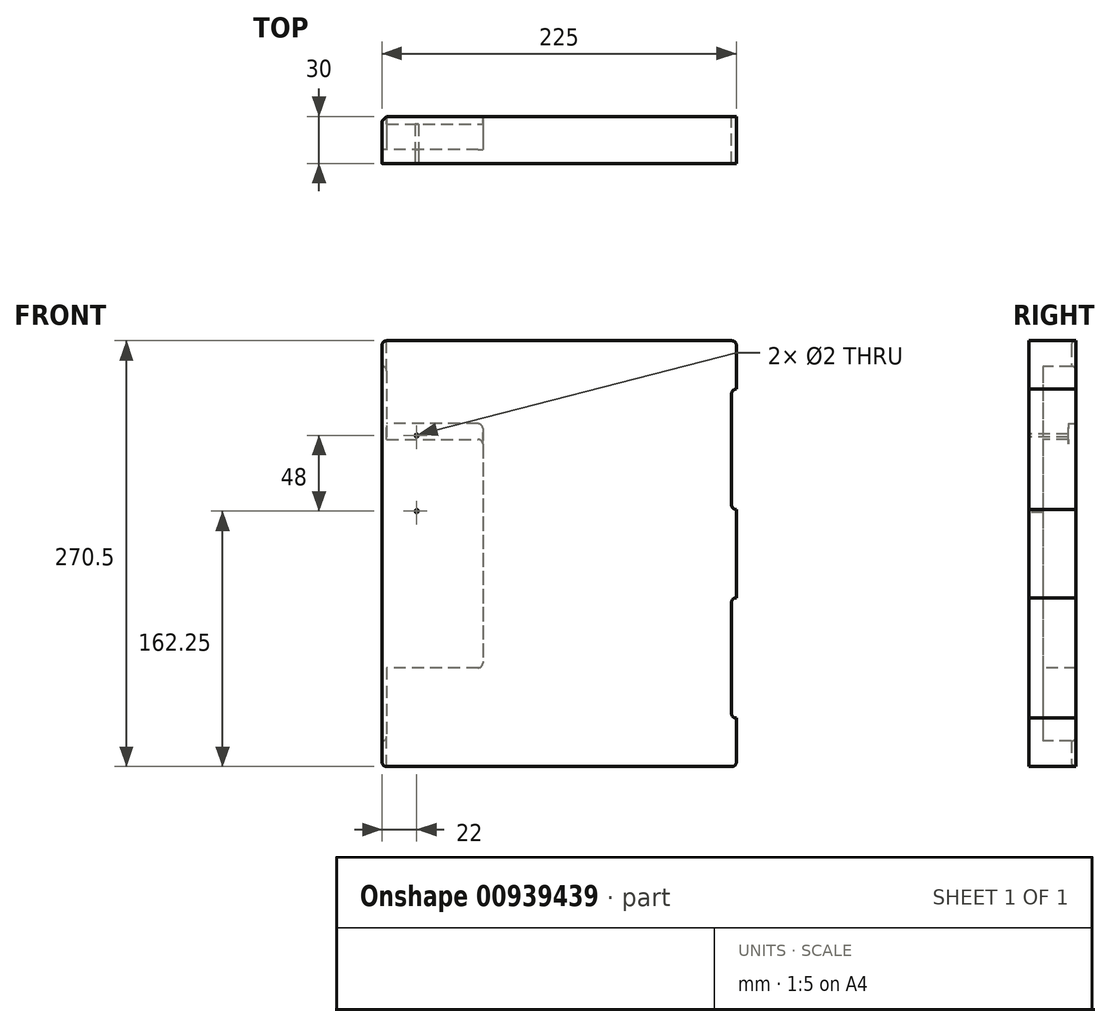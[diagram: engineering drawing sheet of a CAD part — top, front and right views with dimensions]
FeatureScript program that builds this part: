
annotation { "Feature Type Name" : "Feature", "Feature Type Description" : "" }
export const myFeature = defineFeature(function(context is Context, id is Id, definition is map)
    precondition{}
    {
        {
            var Q0;
            Q0=qCreatedBy(makeId("Front.planeOp"),FACE);
            var sketch = newSketch(context, id + "F0", { "sketchPlane" : qUnion([Q0])});
            skLineSegment(sketch, "E0.bottom", {"start": v(-112.5, 135.25) * mm, "end": v(112.5, 135.25) * mm});
            skLineSegment(sketch, "E0.top", {"start": v(-112.5, -135.25) * mm, "end": v(112.5, -135.25) * mm});
            skLineSegment(sketch, "E0.left", {"start": v(-112.5, 135.25) * mm, "end": v(-112.5, -135.25) * mm});
            skLineSegment(sketch, "E0.right", {"start": v(112.5, 135.25) * mm, "end": v(112.5, -135.25) * mm});
            skSolve(sketch);
        }
        {
            var Q0;
            Q0 = qSketchRegion(id + "F0", true);
            extrude(context, id + "F1", {"entities" : qUnion([Q0]), "depth" : 30 * mm, "offsetDistance" : 25 * mm});
        }
        {
            var Q0;
            Q0=makeQuery(id+"F1.opExtrude","SWEPT_EDGE",EDGE,{"disambiguationData":[OSD([sQuery(id+"F0.wireOp",EDGE,"E0.bottom"),sQuery(id+"F0.wireOp",EDGE,"E0.right")])]});
            var Q1;
            Q1=makeQuery(id+"F1.opExtrude","SWEPT_EDGE",EDGE,{"disambiguationData":[OSD([sQuery(id+"F0.wireOp",EDGE,"E0.top"),sQuery(id+"F0.wireOp",EDGE,"E0.right")])]});
            var Q2;
            Q2=makeQuery(id+"F1.opExtrude","SWEPT_EDGE",EDGE,{"disambiguationData":[OSD([sQuery(id+"F0.wireOp",EDGE,"E0.bottom"),sQuery(id+"F0.wireOp",EDGE,"E0.left")])]});
            var Q3;
            Q3=makeQuery(id+"F1.opExtrude","SWEPT_EDGE",EDGE,{"disambiguationData":[OSD([sQuery(id+"F0.wireOp",EDGE,"E0.top"),sQuery(id+"F0.wireOp",EDGE,"E0.left")])]});
            fillet(context, id + "F2", {"entities" : qUnion([Q0, Q1, Q2, Q3]), "radius" : 3 * mm, "tangentPropagation" : true, "allowEdgeOverflow" : false});
        }
        {
            var Q0;
            Q0=makeQuery(id+"F1.opExtrude","SWEPT_FACE",FACE,{"disambiguationData":[OSD([sQuery(id+"F0.wireOp",EDGE,"E0.right")])]});
            var sketch = newSketch(context, id + "F3", { "sketchPlane" : qUnion([Q0])});
            skLineSegment(sketch, "E1.bottom", {"start": v(-30, 104.5) * mm, "end": v(0, 104.5) * mm});
            skLineSegment(sketch, "E1.top", {"start": v(-30, 28) * mm, "end": v(0, 28) * mm});
            skLineSegment(sketch, "E1.left", {"start": v(-30, 104.5) * mm, "end": v(-30, 28) * mm});
            skLineSegment(sketch, "E1.right", {"start": v(0, 104.5) * mm, "end": v(0, 28) * mm});
            skLineSegment(sketch, "E2.bottom", {"start": v(-30, -28) * mm, "end": v(0, -28) * mm});
            skLineSegment(sketch, "E2.top", {"start": v(-30, -104.5) * mm, "end": v(0, -104.5) * mm});
            skLineSegment(sketch, "E2.left", {"start": v(-30, -28) * mm, "end": v(-30, -104.5) * mm});
            skLineSegment(sketch, "E2.right", {"start": v(0, -28) * mm, "end": v(0, -104.5) * mm});
            skSolve(sketch);
        }
        {
            var Q0;
            Q0 = qSketchRegion(id + "F3", true);
            extrude(context, id + "F4", {"entities" : qUnion([Q0]), "operationType" : NewBodyOperationType.REMOVE, "oppositeDirection" : true, "depth" : 3 * mm, "offsetDistance" : 25 * mm});
        }
        {
            var Q0;
            Q0=makeQuery(id+"F4.boolean.opBoolean","COPY",EDGE,{"derivedFrom":makeQuery(id+"F4.opExtrude","CAP_EDGE",EDGE,{"disambiguationData":[OSD([sQuery(id+"F3.wireOp",EDGE,"E1.top")])],"isStart":false})});
            var Q1;
            Q1=makeQuery(id+"F4.boolean.opBoolean","COPY",EDGE,{"derivedFrom":makeQuery(id+"F4.opExtrude","CAP_EDGE",EDGE,{"disambiguationData":[OSD([sQuery(id+"F3.wireOp",EDGE,"E2.top")])],"isStart":false})});
            var Q2;
            Q2=makeQuery(id+"F4.boolean.opBoolean","COPY",EDGE,{"derivedFrom":makeQuery(id+"F4.opExtrude","CAP_EDGE",EDGE,{"disambiguationData":[OSD([sQuery(id+"F3.wireOp",EDGE,"E2.bottom")])],"isStart":false})});
            var Q3;
            Q3=makeQuery(id+"F4.boolean.opBoolean","COPY",EDGE,{"derivedFrom":makeQuery(id+"F4.opExtrude","CAP_EDGE",EDGE,{"disambiguationData":[OSD([sQuery(id+"F3.wireOp",EDGE,"E1.bottom")])],"isStart":false})});
            fillet(context, id + "F5", {"entities" : qUnion([Q0, Q1, Q2, Q3]), "radius" : 3 * mm, "tangentPropagation" : true, "allowEdgeOverflow" : false});
        }
        {
            var Q0;
            Q0=makeQuery(id+"F1.opExtrude","SWEPT_FACE",FACE,{"disambiguationData":[OSD([sQuery(id+"F0.wireOp",EDGE,"E0.left")])]});
            var sketch = newSketch(context, id + "F6", { "sketchPlane" : qUnion([Q0])});
            skLineSegment(sketch, "E3.bottom", {"start": v(0, 119) * mm, "end": v(21, 119) * mm});
            skLineSegment(sketch, "E3.top", {"start": v(0, -119) * mm, "end": v(21, -119) * mm});
            skLineSegment(sketch, "E3.left", {"start": v(0, 119) * mm, "end": v(0, -119) * mm});
            skLineSegment(sketch, "E3.right", {"start": v(21, 119) * mm, "end": v(21, -119) * mm});
            skSolve(sketch);
        }
        {
            var Q0;
            Q0 = qSketchRegion(id + "F6", true);
            extrude(context, id + "F7", {"entities" : qUnion([Q0]), "operationType" : NewBodyOperationType.REMOVE, "oppositeDirection" : true, "depth" : 3 * mm, "offsetDistance" : 25 * mm});
        }
        {
            var Q0;
            Q0=makeQuery(id+"F7.boolean.opBoolean","COPY",EDGE,{"derivedFrom":makeQuery(id+"F7.opExtrude","CAP_EDGE",EDGE,{"disambiguationData":[OSD([sQuery(id+"F6.wireOp",EDGE,"E3.top")])],"isStart":false})});
            var Q1;
            Q1=makeQuery(id+"F7.boolean.opBoolean","COPY",EDGE,{"derivedFrom":makeQuery(id+"F7.opExtrude","CAP_EDGE",EDGE,{"disambiguationData":[OSD([sQuery(id+"F6.wireOp",EDGE,"E3.bottom")])],"isStart":false})});
            fillet(context, id + "F8", {"entities" : qUnion([Q0, Q1]), "radius" : 3 * mm, "tangentPropagation" : true, "allowEdgeOverflow" : false});
        }
        {
            var Q0;
            Q0=makeQuery(id+"F7.boolean.opBoolean","COPY",FACE,{"derivedFrom":makeQuery(id+"F7.opExtrude","CAP_FACE",FACE,{"disambiguationData":[OSD([sQuery(id+"F6.wireOp",EDGE,"E3.bottom"),sQuery(id+"F6.wireOp",EDGE,"E3.top"),sQuery(id+"F6.wireOp",EDGE,"E3.left"),sQuery(id+"F6.wireOp",EDGE,"E3.right")])],"isStart":false})});
            var sketch = newSketch(context, id + "F9", { "sketchPlane" : qUnion([Q0])});
            skLineSegment(sketch, "E4.bottom", {"start": v(0, 72.5) * mm, "end": v(21, 72.5) * mm});
            skLineSegment(sketch, "E4.top", {"start": v(0, -72.5) * mm, "end": v(21, -72.5) * mm});
            skLineSegment(sketch, "E4.left", {"start": v(0, 72.5) * mm, "end": v(0, -72.5) * mm});
            skLineSegment(sketch, "E4.right", {"start": v(21, 72.5) * mm, "end": v(21, -72.5) * mm});
            skSolve(sketch);
        }
        {
            var Q0;
            Q0 = qSketchRegion(id + "F9", true);
            extrude(context, id + "F10", {"entities" : qUnion([Q0]), "operationType" : NewBodyOperationType.REMOVE, "oppositeDirection" : true, "depth" : 61 * mm, "offsetDistance" : 25 * mm});
        }
        {
            var Q0;
            Q0=makeQuery(id+"F10.boolean.opBoolean","COPY",EDGE,{"derivedFrom":makeQuery(id+"F10.opExtrude","CAP_EDGE",EDGE,{"disambiguationData":[OSD([sQuery(id+"F9.wireOp",EDGE,"E4.top")])],"isStart":false})});
            var Q1;
            Q1=makeQuery(id+"F10.boolean.opBoolean","COPY",EDGE,{"derivedFrom":makeQuery(id+"F10.opExtrude","CAP_EDGE",EDGE,{"disambiguationData":[OSD([sQuery(id+"F9.wireOp",EDGE,"E4.bottom")])],"isStart":false})});
            fillet(context, id + "F11", {"entities" : qUnion([Q0, Q1]), "radius" : 3 * mm, "tangentPropagation" : true, "allowEdgeOverflow" : false});
        }
        {
            var Q0;
            {var subQ0=sQuery(id+"F0.wireOp",EDGE,"E0.left");Q0=makeQuery(id+"F7.boolean.opBoolean","SPLIT",EDGE,{"disambiguationData":[TD([makeQuery(id+"F7.opExtrude","SWEPT_FACE",FACE,{"disambiguationData":[OSD([sQuery(id+"F6.wireOp",EDGE,"E3.top")])]})])],"derivedFrom":makeQuery(id+"F1.opExtrude","CAP_EDGE",EDGE,{"disambiguationData":[OSD([subQ0])],"isStart":true})});}
            var Q1;
            {var subQ0=sQuery(id+"F0.wireOp",EDGE,"E0.left");Q1=makeQuery(id+"F7.boolean.opBoolean","SPLIT",EDGE,{"disambiguationData":[TD([makeQuery(id+"F7.opExtrude","SWEPT_FACE",FACE,{"disambiguationData":[OSD([sQuery(id+"F6.wireOp",EDGE,"E3.bottom")])]})])],"derivedFrom":makeQuery(id+"F1.opExtrude","CAP_EDGE",EDGE,{"disambiguationData":[OSD([subQ0])],"isStart":true})});}
            chamfer(context, id + "F12", {"entities" : qUnion([Q0, Q1]), "width" : 3 * mm});
        }
        {
            var Q0;
            Q0=makeQuery(id+"F1.opExtrude","CAP_FACE",FACE,{"disambiguationData":[OSD([sQuery(id+"F0.wireOp",EDGE,"E0.bottom"),sQuery(id+"F0.wireOp",EDGE,"E0.top"),sQuery(id+"F0.wireOp",EDGE,"E0.left"),sQuery(id+"F0.wireOp",EDGE,"E0.right")])],"isStart":true});
            var sketch = newSketch(context, id + "F13", { "sketchPlane" : qUnion([Q0])});
            skLineSegment(sketch, "E5.bottom", {"start": v(48.5, 69.5) * mm, "end": v(109.5, 69.5) * mm});
            skLineSegment(sketch, "E5.top", {"start": v(48.5, 82.5) * mm, "end": v(109.5, 82.5) * mm});
            skLineSegment(sketch, "E5.left", {"start": v(48.5, 69.5) * mm, "end": v(48.5, 82.5) * mm});
            skLineSegment(sketch, "E5.right", {"start": v(109.5, 69.5) * mm, "end": v(109.5, 82.5) * mm});
            skSolve(sketch);
        }
        {
            var Q0;
            Q0 = qSketchRegion(id + "F13", true);
            extrude(context, id + "F14", {"entities" : qUnion([Q0]), "operationType" : NewBodyOperationType.REMOVE, "oppositeDirection" : true, "depth" : 5 * mm, "offsetDistance" : 25 * mm});
        }
        {
            var Q0;
            Q0=makeQuery(id+"F14.boolean.opBoolean","COPY",EDGE,{"derivedFrom":makeQuery(id+"F14.opExtrude","SWEPT_EDGE",EDGE,{"disambiguationData":[OSD([sQuery(id+"F13.wireOp",EDGE,"E5.top"),sQuery(id+"F13.wireOp",EDGE,"E5.left")])]})});
            fillet(context, id + "F15", {"entities" : qUnion([Q0]), "radius" : 3 * mm, "tangentPropagation" : true, "allowEdgeOverflow" : false});
        }
        {
            var Q0;
            Q0=makeQuery(id+"F1.opExtrude","CAP_FACE",FACE,{"disambiguationData":[OSD([sQuery(id+"F0.wireOp",EDGE,"E0.bottom"),sQuery(id+"F0.wireOp",EDGE,"E0.top"),sQuery(id+"F0.wireOp",EDGE,"E0.left"),sQuery(id+"F0.wireOp",EDGE,"E0.right")])],"isStart":false});
            var sketch = newSketch(context, id + "F16", { "sketchPlane" : qUnion([Q0])});
            skCircle(sketch, "E6", {"center": v(-90.5, 75) * mm, "radius": 1 * mm});
            skCircle(sketch, "E7", {"center": v(-90.5, 27) * mm, "radius": 1 * mm});
            skLineSegment(sketch, "E8", {"start": v(-105.57, 92) * mm, "end": v(-22.6, 92) * mm});
            skSolve(sketch);
        }
        {
            var Q0;
            Q0 = qSketchRegion(id + "F16", true);
            extrude(context, id + "F17", {"entities" : qUnion([Q0]), "operationType" : NewBodyOperationType.REMOVE, "oppositeDirection" : true, "depth" : 25 * mm, "offsetDistance" : 25 * mm});
        }
    });
